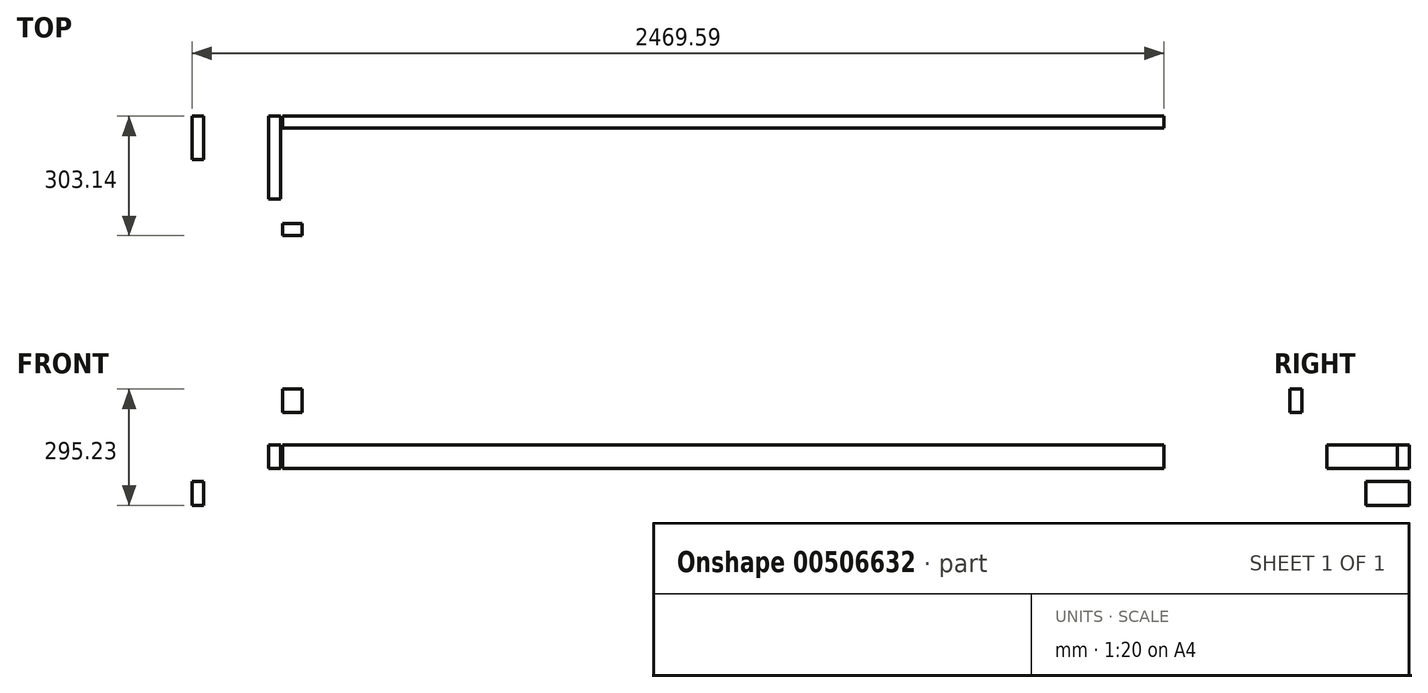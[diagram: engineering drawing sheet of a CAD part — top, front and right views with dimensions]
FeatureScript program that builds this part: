
annotation { "Feature Type Name" : "Feature", "Feature Type Description" : "" }
export const myFeature = defineFeature(function(context is Context, id is Id, definition is map)
    precondition{}
    {
        {
            var Q0;
            Q0=qCreatedBy(makeId("Right.planeOp"),FACE);
            var sketch = newSketch(context, id + "F0", { "sketchPlane" : qUnion([Q0])});
            skLineSegment(sketch, "E0.bottom", {"start": v(-30, 29.87) * mm, "end": v(0, 29.87) * mm});
            skLineSegment(sketch, "E0.top", {"start": v(-30, -30.13) * mm, "end": v(0, -30.13) * mm});
            skLineSegment(sketch, "E0.left", {"start": v(-30, 29.87) * mm, "end": v(-30, -30.13) * mm});
            skLineSegment(sketch, "E0.right", {"start": v(0, 29.87) * mm, "end": v(0, -30.13) * mm});
            skSolve(sketch);
        }
        {
            var Q0;
            Q0=makeQuery(id+"F0.imprint","IMPRINT",FACE,{"disambiguationData":[TD([[makeQuery(id+"F0.imprint","IMPRINT",EDGE,{"derivedFrom":sQuery(id+"F0.wireOp",EDGE,"E0.bottom")}),-1.0]])]});
            extrude(context, id + "F1", {"entities" : qUnion([Q0]), "depth" : 2240 * mm});
        }
        {
            var Q0;
            Q0=qCreatedBy(makeId("Front.planeOp"),FACE);
            var sketch = newSketch(context, id + "F2", { "sketchPlane" : qUnion([Q0])});
            skLineSegment(sketch, "E1.bottom", {"start": v(-35.08, 29.67) * mm, "end": v(-5.08, 29.67) * mm});
            skLineSegment(sketch, "E1.top", {"start": v(-35.08, -30.33) * mm, "end": v(-5.08, -30.33) * mm});
            skLineSegment(sketch, "E1.left", {"start": v(-35.08, 29.67) * mm, "end": v(-35.08, -30.33) * mm});
            skLineSegment(sketch, "E1.right", {"start": v(-5.08, 29.67) * mm, "end": v(-5.08, -30.33) * mm});
            skSolve(sketch);
        }
        {
            var Q0;
            Q0=makeQuery(id+"F2.imprint","IMPRINT",FACE,{"disambiguationData":[TD([[makeQuery(id+"F2.imprint","IMPRINT",EDGE,{"derivedFrom":sQuery(id+"F2.wireOp",EDGE,"E1.bottom")}),-1.0]])]});
            extrude(context, id + "F3", {"entities" : qUnion([Q0]), "depth" : 210 * mm});
        }
        {
            var Q0;
            Q0=qCreatedBy(makeId("Right.planeOp"),FACE);
            var sketch = newSketch(context, id + "F4", { "sketchPlane" : qUnion([Q0])});
            skLineSegment(sketch, "E2.bottom", {"start": v(-303.14, 171.45) * mm, "end": v(-273.14, 171.45) * mm});
            skLineSegment(sketch, "E2.top", {"start": v(-303.14, 111.45) * mm, "end": v(-273.14, 111.45) * mm});
            skLineSegment(sketch, "E2.left", {"start": v(-303.14, 171.45) * mm, "end": v(-303.14, 111.45) * mm});
            skLineSegment(sketch, "E2.right", {"start": v(-273.14, 171.45) * mm, "end": v(-273.14, 111.45) * mm});
            skSolve(sketch);
        }
        {
            var Q0;
            Q0=makeQuery(id+"F4.imprint","IMPRINT",FACE,{"disambiguationData":[TD([[makeQuery(id+"F4.imprint","IMPRINT",EDGE,{"derivedFrom":sQuery(id+"F4.wireOp",EDGE,"E2.bottom")}),-1.0]])]});
            extrude(context, id + "F5", {"entities" : qUnion([Q0]), "depth" : 50 * mm});
        }
        {
            var Q0;
            Q0=qCreatedBy(makeId("Front.planeOp"),FACE);
            var sketch = newSketch(context, id + "F6", { "sketchPlane" : qUnion([Q0])});
            skLineSegment(sketch, "E3.bottom", {"start": v(-229.6, -63.78) * mm, "end": v(-199.6, -63.78) * mm});
            skLineSegment(sketch, "E3.top", {"start": v(-229.6, -123.78) * mm, "end": v(-199.6, -123.78) * mm});
            skLineSegment(sketch, "E3.left", {"start": v(-229.6, -63.78) * mm, "end": v(-229.6, -123.78) * mm});
            skLineSegment(sketch, "E3.right", {"start": v(-199.6, -63.78) * mm, "end": v(-199.6, -123.78) * mm});
            skSolve(sketch);
        }
        {
            var Q0;
            Q0=makeQuery(id+"F6.imprint","IMPRINT",FACE,{"disambiguationData":[TD([[makeQuery(id+"F6.imprint","IMPRINT",EDGE,{"derivedFrom":sQuery(id+"F6.wireOp",EDGE,"E3.bottom")}),-1.0]])]});
            extrude(context, id + "F7", {"entities" : qUnion([Q0]), "depth" : 110 * mm});
        }
    });
